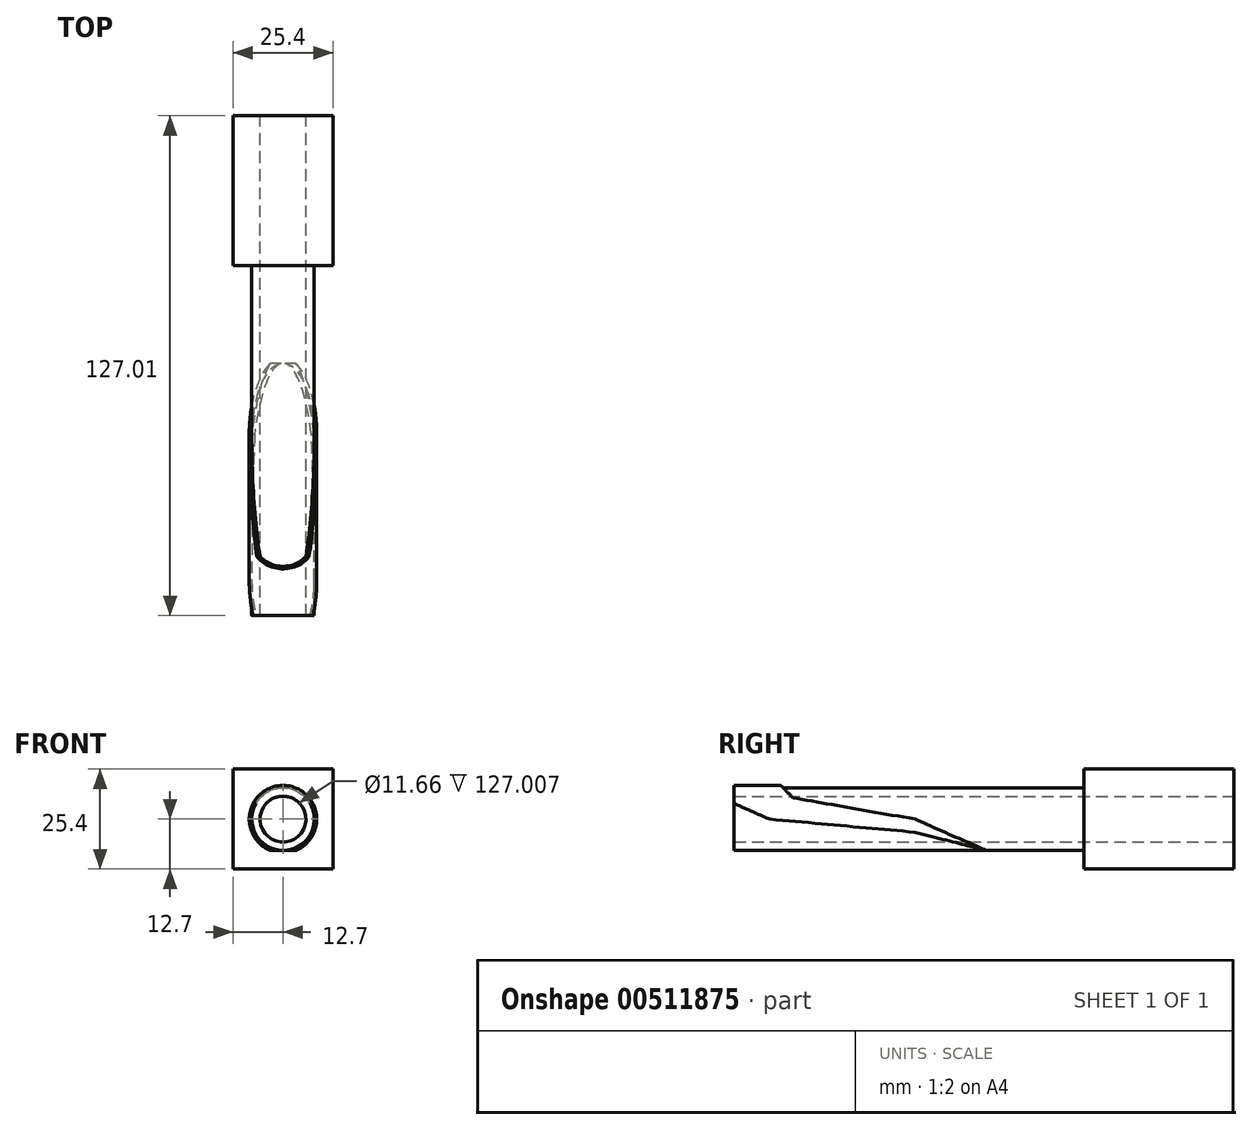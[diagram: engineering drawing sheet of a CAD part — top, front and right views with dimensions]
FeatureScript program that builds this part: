
annotation { "Feature Type Name" : "Feature", "Feature Type Description" : "" }
export const myFeature = defineFeature(function(context is Context, id is Id, definition is map)
    precondition{}
    {
        {
            var Q0;
            Q0=qCreatedBy(makeId("Front.planeOp"),FACE);
            var sketch = newSketch(context, id + "F0", { "sketchPlane" : qUnion([Q0])});
            skLineSegment(sketch, "E0.bottom", {"start": v(12.7, -12.7) * mm, "end": v(-12.7, -12.7) * mm});
            skLineSegment(sketch, "E0.top", {"start": v(12.7, 12.7) * mm, "end": v(-12.7, 12.7) * mm});
            skLineSegment(sketch, "E0.left", {"start": v(12.7, -12.7) * mm, "end": v(12.7, 12.7) * mm});
            skLineSegment(sketch, "E0.right", {"start": v(-12.7, -12.7) * mm, "end": v(-12.7, 12.7) * mm});
            skPoint(sketch, "E0.middle", {"position": v(0, 0) * mm});
            skCircle(sketch, "E1", {"center": v(0, 0) * mm, "radius": 7.94 * mm});
            skCircle(sketch, "E2", {"center": v(0, 0) * mm, "radius": 5.8 * mm});
            skSolve(sketch);
        }
        {
            var Q0;
            Q0=qSketchRegion(id+"F0",true);
            var Q1;
            Q1=makeQuery(id+"F0.imprint","IMPRINT",FACE,{"disambiguationData":[TD([[makeQuery(id+"F0.imprint","IMPRINT",EDGE,{"derivedFrom":sQuery(id+"F0.wireOp",EDGE,"E1")}),1.0]])]});
            extrude(context, id + "F1", {"entities" : qUnion([Q0, Q1]), "depth" : 38.1 * mm});
        }
        {
            var Q0;
            Q0=makeQuery(id+"F0.imprint","IMPRINT",FACE,{"disambiguationData":[TD([[makeQuery(id+"F0.imprint","IMPRINT",EDGE,{"derivedFrom":sQuery(id+"F0.wireOp",EDGE,"E1")}),1.0]])]});
            extrude(context, id + "F2", {"entities" : qUnion([Q0]), "operationType" : NewBodyOperationType.ADD, "depth" : 127 * mm, "offsetDistance" : 25.4 * mm});
        }
        {
            var Q0;
            Q0=makeQuery(id+"F2.opExtrude","CAP_FACE",FACE,{"disambiguationData":[OSD([sQuery(id+"F0.wireOp",EDGE,"E1")])],"isStart":false});
            var sketch = newSketch(context, id + "F3", { "sketchPlane" : qUnion([Q0])});
            skCircle(sketch, "E3", {"center": v(9.58, 0) * mm, "radius": 2.46 * mm});
            skCircle(sketch, "E4.1.0", {"center": v(5.97, 7.49) * mm, "radius": 2.46 * mm});
            skCircle(sketch, "E4.2.0", {"center": v(-2.13, 9.34) * mm, "radius": 2.46 * mm});
            skCircle(sketch, "E4.3.0", {"center": v(-8.63, 4.16) * mm, "radius": 2.46 * mm});
            skCircle(sketch, "E4.4.0", {"center": v(-8.63, -4.16) * mm, "radius": 2.46 * mm});
            skCircle(sketch, "E4.5.0", {"center": v(-2.13, -9.34) * mm, "radius": 2.46 * mm});
            skCircle(sketch, "E4.6.0", {"center": v(5.97, -7.49) * mm, "radius": 2.46 * mm});
            skPoint(sketch, "E4.center", {"position": v(0, 0) * mm});
            skSolve(sketch);
        }
        {
            var Q0;
            Q0=qCreatedBy(makeId("Right.planeOp"),FACE);
            var sketch = newSketch(context, id + "F4", { "sketchPlane" : qUnion([Q0])});
            skLineSegment(sketch, "E5", {"start": v(-131.1, 5.81) * mm, "end": v(-118, 0) * mm});
            skLineSegment(sketch, "E6", {"start": v(-118, 0) * mm, "end": v(-81.02, -3.31) * mm});
            skLineSegment(sketch, "E7", {"start": v(-81.02, -3.31) * mm, "end": v(-62.97, -7.92) * mm});
            skLineSegment(sketch, "E8", {"start": v(-126.56, 20.13) * mm, "end": v(-111.99, 5.4) * mm});
            skLineSegment(sketch, "E9", {"start": v(-111.99, 5.4) * mm, "end": v(-81.02, 0) * mm});
            skLineSegment(sketch, "E10", {"start": v(-81.02, 0) * mm, "end": v(-62.97, -7.92) * mm});
            skLineSegment(sketch, "E11", {"start": v(-126.56, 20.13) * mm, "end": v(-131.1, 5.81) * mm});
            skSolve(sketch);
        }
        {
            var Q0;
            Q0 = qSketchRegion(id + "F4", true);
            extrude(context, id + "F5", {"entities" : qUnion([Q0]), "operationType" : NewBodyOperationType.ADD, "depth" : 18.95 * mm, "offsetDistance" : 25.4 * mm, "hasSecondDirection" : true, "secondDirectionOppositeDirection" : true, "secondDirectionDepth" : 19.54 * mm});
        }
        {
            var Q0;
            Q0=makeQuery(id+"F2.opExtrude","CAP_FACE",FACE,{"disambiguationData":[OSD([sQuery(id+"F0.wireOp",EDGE,"E1"),sQuery(id+"F0.wireOp",EDGE,"E2")])],"isStart":false});
            var sketch = newSketch(context, id + "F6", { "sketchPlane" : qUnion([Q0])});
            skCircle(sketch, "E12", {"center": v(0, 0) * mm, "radius": 8.57 * mm});
            skCircle(sketch, "E13", {"center": v(0, 0) * mm, "radius": 38.1 * mm});
            skSolve(sketch);
        }
        {
            var Q0;
            Q0 = qSketchRegion(id + "F6", true);
            extrude(context, id + "F7", {"entities" : qUnion([Q0]), "operationType" : NewBodyOperationType.REMOVE, "oppositeDirection" : true, "depth" : 78.32 * mm, "offsetDistance" : 25.4 * mm, "hasSecondDirection" : true, "secondDirectionOppositeDirection" : false, "secondDirectionDepth" : 39.14 * mm});
        }
        {
            var Q0;
            Q0=makeQuery(id+"F1.opExtrude","CAP_FACE",FACE,{"disambiguationData":[OSD([sQuery(id+"F0.wireOp",EDGE,"E0.bottom"),sQuery(id+"F0.wireOp",EDGE,"E0.top"),sQuery(id+"F0.wireOp",EDGE,"E0.left"),sQuery(id+"F0.wireOp",EDGE,"E0.right"),sQuery(id+"F0.wireOp",EDGE,"E2")])],"isStart":true});
            var sketch = newSketch(context, id + "F8", { "sketchPlane" : qUnion([Q0])});
            skCircle(sketch, "E14", {"center": v(0, 0) * mm, "radius": 5.83 * mm});
            skSolve(sketch);
        }
        {
            var Q0;
            Q0 = qSketchRegion(id + "F8", true);
            extrude(context, id + "F9", {"entities" : qUnion([Q0]), "operationType" : NewBodyOperationType.REMOVE, "oppositeDirection" : true, "depth" : 152.4 * mm, "offsetDistance" : 25.4 * mm});
        }
        {
            var Q0;
            Q0=qCreatedBy(makeId("Right.planeOp"),FACE);
            var sketch = newSketch(context, id + "F10", { "sketchPlane" : qUnion([Q0])});
            skLineSegment(sketch, "E15", {"start": v(-127, -9.19) * mm, "end": v(-127, 11.7) * mm});
            skLineSegment(sketch, "E16", {"start": v(-127, 11.7) * mm, "end": v(-133.47, 11.7) * mm});
            skLineSegment(sketch, "E17", {"start": v(-133.47, 11.7) * mm, "end": v(-127, -9.19) * mm});
            skSolve(sketch);
        }
        {
            var Q0;
            Q0 = qSketchRegion(id + "F10", true);
            extrude(context, id + "F11", {"entities" : qUnion([Q0]), "operationType" : NewBodyOperationType.REMOVE, "oppositeDirection" : true, "depth" : 25.4 * mm, "offsetDistance" : 25.4 * mm, "hasSecondDirection" : true, "secondDirectionOppositeDirection" : false, "secondDirectionDepth" : 25.4 * mm});
        }
    });
